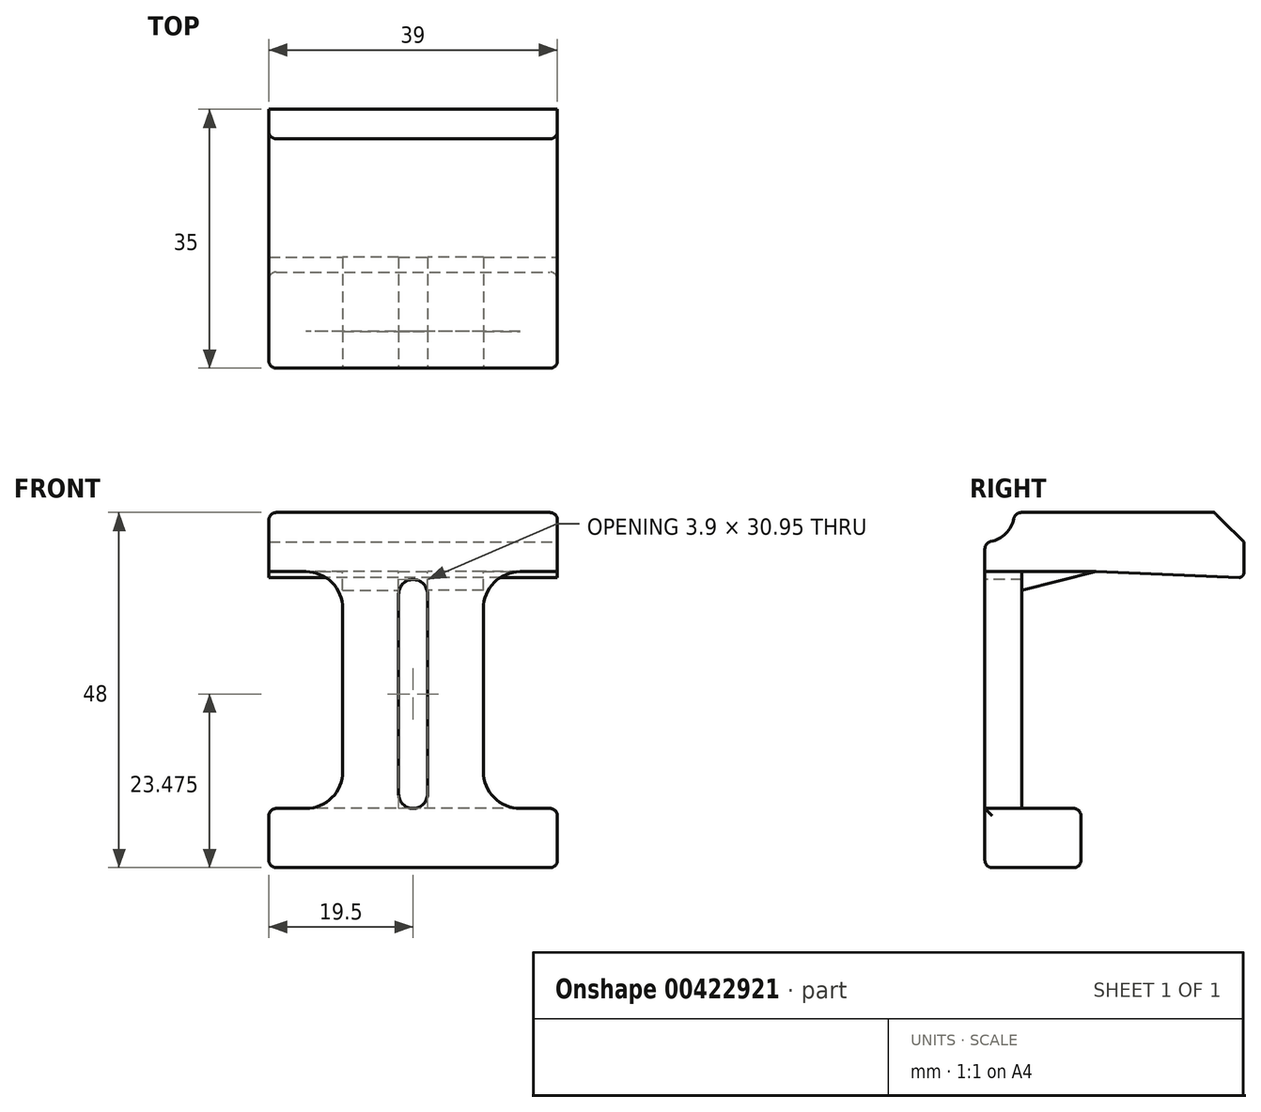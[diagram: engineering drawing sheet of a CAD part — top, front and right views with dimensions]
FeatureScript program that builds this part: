
annotation { "Feature Type Name" : "Feature", "Feature Type Description" : "" }
export const myFeature = defineFeature(function(context is Context, id is Id, definition is map)
    precondition{}
    {
        {
            var Q0;
            Q0=qCreatedBy(makeId("Front.planeOp"),FACE);
            var sketch = newSketch(context, id + "F0", { "sketchPlane" : qUnion([Q0])});
            skLineSegment(sketch, "E0.bottom", {"start": v(-25, 24) * mm, "end": v(14, 24) * mm});
            skLineSegment(sketch, "E0.top", {"start": v(-25, -24) * mm, "end": v(14, -24) * mm});
            skLineSegment(sketch, "E0.left", {"start": v(-25, 24) * mm, "end": v(-25, -24) * mm});
            skLineSegment(sketch, "E0.right", {"start": v(14, 24) * mm, "end": v(14, -24) * mm});
            skSolve(sketch);
        }
        {
            var Q0;
            Q0 = qSketchRegion(id + "F0", true);
            extrude(context, id + "F1", {"entities" : qUnion([Q0]), "depth" : 5 * mm});
        }
        {
            var Q0;
            Q0=makeQuery(id+"F1.opExtrude","CAP_FACE",FACE,{"disambiguationData":[OSD([sQuery(id+"F0.wireOp",EDGE,"E0.bottom"),sQuery(id+"F0.wireOp",EDGE,"E0.top"),sQuery(id+"F0.wireOp",EDGE,"E0.left"),sQuery(id+"F0.wireOp",EDGE,"E0.right")])],"isStart":false});
            var sketch = newSketch(context, id + "F2", { "sketchPlane" : qUnion([Q0])});
            skLineSegment(sketch, "E1.bottom", {"start": v(-25, 16) * mm, "end": v(-15, 16) * mm});
            skLineSegment(sketch, "E1.top", {"start": v(-25, -16) * mm, "end": v(-15, -16) * mm});
            skLineSegment(sketch, "E1.left", {"start": v(-25, 16) * mm, "end": v(-25, -16) * mm});
            skLineSegment(sketch, "E1.right", {"start": v(-15, 16) * mm, "end": v(-15, -16) * mm});
            skLineSegment(sketch, "E2.bottom", {"start": v(14, 16) * mm, "end": v(4, 16) * mm});
            skLineSegment(sketch, "E2.top", {"start": v(14, -16) * mm, "end": v(4, -16) * mm});
            skLineSegment(sketch, "E2.left", {"start": v(14, 16) * mm, "end": v(14, -16) * mm});
            skLineSegment(sketch, "E2.right", {"start": v(4, 16) * mm, "end": v(4, -16) * mm});
            skSolve(sketch);
        }
        {
            var Q0;
            Q0 = qSketchRegion(id + "F2", true);
            extrude(context, id + "F3", {"entities" : qUnion([Q0]), "operationType" : NewBodyOperationType.REMOVE, "endBound" : BoundingType.THROUGH_ALL, "oppositeDirection" : true, "depth" : 25 * mm});
        }
        {
            var Q0;
            Q0=makeQuery(id+"F1.opExtrude","CAP_FACE",FACE,{"disambiguationData":[OSD([sQuery(id+"F0.wireOp",EDGE,"E0.bottom"),sQuery(id+"F0.wireOp",EDGE,"E0.top"),sQuery(id+"F0.wireOp",EDGE,"E0.left"),sQuery(id+"F0.wireOp",EDGE,"E0.right")])],"isStart":true});
            var sketch = newSketch(context, id + "F4", { "sketchPlane" : qUnion([Q0])});
            skLineSegment(sketch, "E3.bottom", {"start": v(-14, 16) * mm, "end": v(25, 16) * mm});
            skLineSegment(sketch, "E3.top", {"start": v(-14, 24) * mm, "end": v(25, 24) * mm});
            skLineSegment(sketch, "E3.left", {"start": v(-14, 16) * mm, "end": v(-14, 24) * mm});
            skLineSegment(sketch, "E3.right", {"start": v(25, 16) * mm, "end": v(25, 24) * mm});
            skSolve(sketch);
        }
        {
            var Q0;
            Q0 = qSketchRegion(id + "F4", true);
            extrude(context, id + "F5", {"entities" : qUnion([Q0]), "operationType" : NewBodyOperationType.ADD, "depth" : 30 * mm});
        }
        {
            var Q0;
            {var subQ0=sQuery(id+"F0.wireOp",EDGE,"E0.bottom");var subQ1=sQuery(id+"F0.wireOp",EDGE,"E0.right");Q0=makeQuery(id+"F5.boolean.opBoolean","MERGE",FACE,{"derivedFrom":[makeQuery(id+"F3.boolean.opBoolean","SPLIT",FACE,{"disambiguationData":[TD([makeQuery(id+"F1.opExtrude","SWEPT_FACE",FACE,{"disambiguationData":[OSD([subQ0])]})])],"derivedFrom":makeQuery(id+"F1.opExtrude","SWEPT_FACE",FACE,{"disambiguationData":[OSD([subQ1])]})}),makeQuery(id+"F5.opExtrude","SWEPT_FACE",FACE,{"disambiguationData":[OSD([sQuery(id+"F4.wireOp",EDGE,"E3.left")])]})]});}
            var sketch = newSketch(context, id + "F6", { "sketchPlane" : qUnion([Q0])});
            skLineSegment(sketch, "E4", {"start": v(10, 16) * mm, "end": v(30, 16) * mm});
            skLineSegment(sketch, "E5", {"start": v(30, 16) * mm, "end": v(30, 15.2) * mm});
            skLineSegment(sketch, "E6", {"start": v(30, 15.2) * mm, "end": v(10, 16) * mm});
            skSolve(sketch);
        }
        {
            var Q0;
            Q0 = qSketchRegion(id + "F6", true);
            var Q1;
            {var subQ0=sQuery(id+"F0.wireOp",EDGE,"E0.bottom");var subQ2=sQuery(id+"F0.wireOp",EDGE,"E0.left");Q1=makeQuery(id+"F5.boolean.opBoolean","MERGE",FACE,{"derivedFrom":[makeQuery(id+"F3.boolean.opBoolean","SPLIT",FACE,{"disambiguationData":[TD([makeQuery(id+"F1.opExtrude","SWEPT_FACE",FACE,{"disambiguationData":[OSD([subQ0])]})])],"derivedFrom":makeQuery(id+"F1.opExtrude","SWEPT_FACE",FACE,{"disambiguationData":[OSD([subQ2])]})}),makeQuery(id+"F5.opExtrude","SWEPT_FACE",FACE,{"disambiguationData":[OSD([sQuery(id+"F4.wireOp",EDGE,"E3.right")])]})]});}
            extrude(context, id + "F7", {"entities" : qUnion([Q0]), "operationType" : NewBodyOperationType.ADD, "endBound" : BoundingType.UP_TO_SURFACE, "oppositeDirection" : true, "endBoundEntityFace" : qUnion([Q1]), "depth" : 25 * mm});
        }
        {
            var Q0;
            {var subQ0=sQuery(id+"F0.wireOp",EDGE,"E0.bottom");var subQ1=sQuery(id+"F0.wireOp",EDGE,"E0.right");Q0=makeQuery(id+"F7.boolean.opBoolean","MERGE",FACE,{"derivedFrom":[makeQuery(id+"F5.boolean.opBoolean","MERGE",FACE,{"derivedFrom":[makeQuery(id+"F3.boolean.opBoolean","SPLIT",FACE,{"disambiguationData":[TD([makeQuery(id+"F1.opExtrude","SWEPT_FACE",FACE,{"disambiguationData":[OSD([subQ0])]})])],"derivedFrom":makeQuery(id+"F1.opExtrude","SWEPT_FACE",FACE,{"disambiguationData":[OSD([subQ1])]})}),makeQuery(id+"F5.opExtrude","SWEPT_FACE",FACE,{"disambiguationData":[OSD([sQuery(id+"F4.wireOp",EDGE,"E3.left")])]})]}),makeQuery(id+"F7.opExtrude","CAP_FACE",FACE,{"disambiguationData":[OSD([sQuery(id+"F6.wireOp",EDGE,"E4"),sQuery(id+"F6.wireOp",EDGE,"E5"),sQuery(id+"F6.wireOp",EDGE,"E6")])],"isStart":true})]});}
            var sketch = newSketch(context, id + "F8", { "sketchPlane" : qUnion([Q0])});
            skCircle(sketch, "E7", {"center": v(-5, 24) * mm, "radius": 4 * mm});
            skSolve(sketch);
        }
        {
            var Q0;
            Q0 = qSketchRegion(id + "F8", true);
            extrude(context, id + "F9", {"entities" : qUnion([Q0]), "operationType" : NewBodyOperationType.REMOVE, "endBound" : BoundingType.THROUGH_ALL, "oppositeDirection" : true, "depth" : 25 * mm});
        }
        {
            var Q0;
            Q0=makeQuery(id+"F9.boolean.opBoolean","INTERSECT",EDGE,{"derivedFrom":[makeQuery(id+"F5.boolean.opBoolean","MERGE",FACE,{"derivedFrom":[makeQuery(id+"F1.opExtrude","SWEPT_FACE",FACE,{"disambiguationData":[OSD([sQuery(id+"F0.wireOp",EDGE,"E0.bottom")])]}),makeQuery(id+"F5.opExtrude","SWEPT_FACE",FACE,{"disambiguationData":[OSD([sQuery(id+"F4.wireOp",EDGE,"E3.top")])]})]}),makeQuery(id+"F9.opExtrude","SWEPT_FACE",FACE,{"disambiguationData":[OSD([sQuery(id+"F8.wireOp",EDGE,"E7")])]})]});
            var Q1;
            Q1=makeQuery(id+"F9.boolean.opBoolean","INTERSECT",EDGE,{"derivedFrom":[makeQuery(id+"F1.opExtrude","CAP_FACE",FACE,{"disambiguationData":[OSD([sQuery(id+"F0.wireOp",EDGE,"E0.bottom"),sQuery(id+"F0.wireOp",EDGE,"E0.top"),sQuery(id+"F0.wireOp",EDGE,"E0.left"),sQuery(id+"F0.wireOp",EDGE,"E0.right")])],"isStart":false}),makeQuery(id+"F9.opExtrude","SWEPT_FACE",FACE,{"disambiguationData":[OSD([sQuery(id+"F8.wireOp",EDGE,"E7")])]})]});
            fillet(context, id + "F10", {"entities" : qUnion([Q0, Q1]), "radius" : 1 * mm, "tangentPropagation" : true, "allowEdgeOverflow" : false});
        }
        {
            var Q0;
            Q0=makeQuery(id+"F5.opExtrude","CAP_EDGE",EDGE,{"disambiguationData":[OSD([sQuery(id+"F4.wireOp",EDGE,"E3.top")])],"isStart":false});
            chamfer(context, id + "F11", {"entities" : qUnion([Q0]), "width" : 4 * mm, "tangentPropagation" : true});
        }
        {
            var Q0;
            Q0=makeQuery(id+"F1.opExtrude","CAP_FACE",FACE,{"disambiguationData":[OSD([sQuery(id+"F0.wireOp",EDGE,"E0.bottom"),sQuery(id+"F0.wireOp",EDGE,"E0.top"),sQuery(id+"F0.wireOp",EDGE,"E0.left"),sQuery(id+"F0.wireOp",EDGE,"E0.right")])],"isStart":true});
            var sketch = newSketch(context, id + "F12", { "sketchPlane" : qUnion([Q0])});
            skLineSegment(sketch, "E8.bottom", {"start": v(-14, -16) * mm, "end": v(25, -16) * mm});
            skLineSegment(sketch, "E8.top", {"start": v(-14, -24) * mm, "end": v(25, -24) * mm});
            skLineSegment(sketch, "E8.left", {"start": v(-14, -16) * mm, "end": v(-14, -24) * mm});
            skLineSegment(sketch, "E8.right", {"start": v(25, -16) * mm, "end": v(25, -24) * mm});
            skSolve(sketch);
        }
        {
            var Q0;
            Q0 = qSketchRegion(id + "F12", true);
            extrude(context, id + "F13", {"entities" : qUnion([Q0]), "operationType" : NewBodyOperationType.ADD, "depth" : 8 * mm});
        }
        {
            var Q0;
            Q0=makeQuery(id+"F1.opExtrude","CAP_FACE",FACE,{"disambiguationData":[OSD([sQuery(id+"F0.wireOp",EDGE,"E0.bottom"),sQuery(id+"F0.wireOp",EDGE,"E0.top"),sQuery(id+"F0.wireOp",EDGE,"E0.left"),sQuery(id+"F0.wireOp",EDGE,"E0.right")])],"isStart":false});
            var sketch = newSketch(context, id + "F14", { "sketchPlane" : qUnion([Q0])});
            skArc(sketch, "E9", {"start": v(-3.55, 13) * mm, "mid": v(-5.5, 14.95) * mm, "end": v(-7.45, 13) * mm});
            skArc(sketch, "E10", {"start": v(-7.45, -14.05) * mm, "mid": v(-5.5, -16) * mm, "end": v(-3.55, -14.05) * mm});
            skLineSegment(sketch, "E11", {"start": v(-3.55, 13) * mm, "end": v(-3.55, -14.05) * mm});
            skLineSegment(sketch, "E12", {"start": v(-7.45, 13) * mm, "end": v(-7.45, -14.05) * mm});
            skSolve(sketch);
        }
        {
            var Q0;
            Q0 = qSketchRegion(id + "F14", true);
            extrude(context, id + "F15", {"entities" : qUnion([Q0]), "operationType" : NewBodyOperationType.REMOVE, "endBound" : BoundingType.THROUGH_ALL, "oppositeDirection" : true, "depth" : 25 * mm});
        }
        {
            var Q0;
            Q0=makeQuery(id+"F1.opExtrude","CAP_EDGE",EDGE,{"disambiguationData":[OSD([sQuery(id+"F0.wireOp",EDGE,"E0.bottom")])],"isStart":false});
            var Q1;
            Q1=makeQuery(id+"F1.opExtrude","CAP_EDGE",EDGE,{"disambiguationData":[OSD([sQuery(id+"F0.wireOp",EDGE,"E0.top")])],"isStart":false});
            var Q2;
            {var subQ0=sQuery(id+"F0.wireOp",EDGE,"E0.left");var subQ1=sQuery(id+"F0.wireOp",EDGE,"E0.top");Q2=makeQuery(id+"F3.boolean.opBoolean","SPLIT",EDGE,{"disambiguationData":[TD([makeQuery(id+"F1.opExtrude","SWEPT_FACE",FACE,{"disambiguationData":[OSD([subQ1])]})])],"derivedFrom":makeQuery(id+"F1.opExtrude","CAP_EDGE",EDGE,{"disambiguationData":[OSD([subQ0])],"isStart":false})});}
            var Q3;
            {var subQ0=sQuery(id+"F0.wireOp",EDGE,"E0.right");var subQ1=sQuery(id+"F0.wireOp",EDGE,"E0.top");Q3=makeQuery(id+"F3.boolean.opBoolean","SPLIT",EDGE,{"disambiguationData":[TD([makeQuery(id+"F1.opExtrude","SWEPT_FACE",FACE,{"disambiguationData":[OSD([subQ1])]})])],"derivedFrom":makeQuery(id+"F1.opExtrude","CAP_EDGE",EDGE,{"disambiguationData":[OSD([subQ0])],"isStart":false})});}
            var Q4;
            {var subQ0=sQuery(id+"F0.wireOp",EDGE,"E0.bottom");var subQ1=sQuery(id+"F0.wireOp",EDGE,"E0.right");Q4=makeQuery(id+"F3.boolean.opBoolean","SPLIT",EDGE,{"disambiguationData":[TD([makeQuery(id+"F1.opExtrude","SWEPT_FACE",FACE,{"disambiguationData":[OSD([subQ0])]})])],"derivedFrom":makeQuery(id+"F1.opExtrude","CAP_EDGE",EDGE,{"disambiguationData":[OSD([subQ1])],"isStart":false})});}
            var Q5;
            {var subQ0=sQuery(id+"F0.wireOp",EDGE,"E0.bottom");var subQ1=sQuery(id+"F0.wireOp",EDGE,"E0.left");Q5=makeQuery(id+"F3.boolean.opBoolean","SPLIT",EDGE,{"disambiguationData":[TD([makeQuery(id+"F1.opExtrude","SWEPT_FACE",FACE,{"disambiguationData":[OSD([subQ0])]})])],"derivedFrom":makeQuery(id+"F1.opExtrude","CAP_EDGE",EDGE,{"disambiguationData":[OSD([subQ1])],"isStart":false})});}
            var Q6;
            Q6=makeQuery(id+"F5.boolean.opBoolean","MERGE",EDGE,{"derivedFrom":[makeQuery(id+"F1.opExtrude","SWEPT_EDGE",EDGE,{"disambiguationData":[OSD([sQuery(id+"F0.wireOp",EDGE,"E0.bottom"),sQuery(id+"F0.wireOp",EDGE,"E0.left")])]}),makeQuery(id+"F5.opExtrude","SWEPT_EDGE",EDGE,{"disambiguationData":[OSD([sQuery(id+"F4.wireOp",EDGE,"E3.top"),sQuery(id+"F4.wireOp",EDGE,"E3.right")])]})]});
            var Q7;
            Q7=makeQuery(id+"F5.boolean.opBoolean","MERGE",EDGE,{"derivedFrom":[makeQuery(id+"F1.opExtrude","SWEPT_EDGE",EDGE,{"disambiguationData":[OSD([sQuery(id+"F0.wireOp",EDGE,"E0.bottom"),sQuery(id+"F0.wireOp",EDGE,"E0.right")])]}),makeQuery(id+"F5.opExtrude","SWEPT_EDGE",EDGE,{"disambiguationData":[OSD([sQuery(id+"F4.wireOp",EDGE,"E3.top"),sQuery(id+"F4.wireOp",EDGE,"E3.left")])]})]});
            var Q8;
            Q8=makeQuery(id+"F13.boolean.opBoolean","MERGE",EDGE,{"derivedFrom":[makeQuery(id+"F1.opExtrude","SWEPT_EDGE",EDGE,{"disambiguationData":[OSD([sQuery(id+"F0.wireOp",EDGE,"E0.top"),sQuery(id+"F0.wireOp",EDGE,"E0.right")])]}),makeQuery(id+"F13.opExtrude","SWEPT_EDGE",EDGE,{"disambiguationData":[OSD([sQuery(id+"F12.wireOp",EDGE,"E8.top"),sQuery(id+"F12.wireOp",EDGE,"E8.left")])]})]});
            var Q9;
            Q9=makeQuery(id+"F13.boolean.opBoolean","MERGE",EDGE,{"derivedFrom":[makeQuery(id+"F1.opExtrude","SWEPT_EDGE",EDGE,{"disambiguationData":[OSD([sQuery(id+"F0.wireOp",EDGE,"E0.top"),sQuery(id+"F0.wireOp",EDGE,"E0.left")])]}),makeQuery(id+"F13.opExtrude","SWEPT_EDGE",EDGE,{"disambiguationData":[OSD([sQuery(id+"F12.wireOp",EDGE,"E8.top"),sQuery(id+"F12.wireOp",EDGE,"E8.right")])]})]});
            var Q10;
            Q10=makeQuery(id+"F13.opExtrude","CAP_EDGE",EDGE,{"disambiguationData":[OSD([sQuery(id+"F12.wireOp",EDGE,"E8.bottom")])],"isStart":false});
            var Q11;
            Q11=makeQuery(id+"F13.opExtrude","CAP_EDGE",EDGE,{"disambiguationData":[OSD([sQuery(id+"F12.wireOp",EDGE,"E8.top")])],"isStart":false});
            var Q12;
            Q12=makeQuery(id+"F13.opExtrude","CAP_EDGE",EDGE,{"disambiguationData":[OSD([sQuery(id+"F12.wireOp",EDGE,"E8.left")])],"isStart":false});
            var Q13;
            Q13=makeQuery(id+"F13.opExtrude","CAP_EDGE",EDGE,{"disambiguationData":[OSD([sQuery(id+"F12.wireOp",EDGE,"E8.right")])],"isStart":false});
            var Q14;
            Q14=makeQuery(id+"F13.boolean.opBoolean","MERGE",EDGE,{"derivedFrom":[makeQuery(id+"F3.boolean.opBoolean","COPY",EDGE,{"derivedFrom":makeQuery(id+"F3.opExtrude","SWEPT_EDGE",EDGE,{"disambiguationData":[OSD([sQuery(id+"F0.wireOp",EDGE,"E0.left"),sQuery(id+"F2.wireOp",EDGE,"E1.top"),sQuery(id+"F2.wireOp",EDGE,"E1.left")])]})}),makeQuery(id+"F13.opExtrude","SWEPT_EDGE",EDGE,{"disambiguationData":[OSD([sQuery(id+"F12.wireOp",EDGE,"E8.bottom"),sQuery(id+"F12.wireOp",EDGE,"E8.right")])]})]});
            var Q15;
            Q15=makeQuery(id+"F13.boolean.opBoolean","MERGE",EDGE,{"derivedFrom":[makeQuery(id+"F3.boolean.opBoolean","COPY",EDGE,{"derivedFrom":makeQuery(id+"F3.opExtrude","SWEPT_EDGE",EDGE,{"disambiguationData":[OSD([sQuery(id+"F0.wireOp",EDGE,"E0.right"),sQuery(id+"F2.wireOp",EDGE,"E2.top"),sQuery(id+"F2.wireOp",EDGE,"E2.left")])]})}),makeQuery(id+"F13.opExtrude","SWEPT_EDGE",EDGE,{"disambiguationData":[OSD([sQuery(id+"F12.wireOp",EDGE,"E8.bottom"),sQuery(id+"F12.wireOp",EDGE,"E8.left")])]})]});
            fillet(context, id + "F16", {"entities" : qUnion([Q0, Q1, Q2, Q3, Q4, Q5, Q6, Q7, Q8, Q9, Q10, Q11, Q12, Q13, Q14, Q15]), "radius" : 1 * mm, "tangentPropagation" : true, "allowEdgeOverflow" : false});
        }
        {
            var Q0;
            Q0=makeQuery(id+"F3.boolean.opBoolean","COPY",EDGE,{"derivedFrom":makeQuery(id+"F3.opExtrude","SWEPT_EDGE",EDGE,{"disambiguationData":[OSD([sQuery(id+"F2.wireOp",EDGE,"E1.bottom"),sQuery(id+"F2.wireOp",EDGE,"E1.right")])]})});
            var Q1;
            Q1=makeQuery(id+"F3.boolean.opBoolean","COPY",EDGE,{"derivedFrom":makeQuery(id+"F3.opExtrude","SWEPT_EDGE",EDGE,{"disambiguationData":[OSD([sQuery(id+"F2.wireOp",EDGE,"E1.top"),sQuery(id+"F2.wireOp",EDGE,"E1.right")])]})});
            var Q2;
            Q2=makeQuery(id+"F3.boolean.opBoolean","COPY",EDGE,{"derivedFrom":makeQuery(id+"F3.opExtrude","SWEPT_EDGE",EDGE,{"disambiguationData":[OSD([sQuery(id+"F2.wireOp",EDGE,"E2.bottom"),sQuery(id+"F2.wireOp",EDGE,"E2.right")])]})});
            var Q3;
            Q3=makeQuery(id+"F3.boolean.opBoolean","COPY",EDGE,{"derivedFrom":makeQuery(id+"F3.opExtrude","SWEPT_EDGE",EDGE,{"disambiguationData":[OSD([sQuery(id+"F2.wireOp",EDGE,"E2.top"),sQuery(id+"F2.wireOp",EDGE,"E2.right")])]})});
            fillet(context, id + "F17", {"entities" : qUnion([Q0, Q1, Q2, Q3]), "radius" : 5 * mm, "tangentPropagation" : true, "allowEdgeOverflow" : false});
        }
        {
            var Q0;
            Q0=makeQuery(id+"F7.opExtrude","SWEPT_EDGE",EDGE,{"disambiguationData":[OSD([sQuery(id+"F6.wireOp",EDGE,"E5"),sQuery(id+"F6.wireOp",EDGE,"E6")])]});
            fillet(context, id + "F18", {"entities" : qUnion([Q0]), "radius" : .6 * mm, "tangentPropagation" : true, "allowEdgeOverflow" : false});
        }
        {
            var Q0;
            Q0=makeQuery(id+"F1.opExtrude","CAP_FACE",FACE,{"disambiguationData":[OSD([sQuery(id+"F0.wireOp",EDGE,"E0.bottom"),sQuery(id+"F0.wireOp",EDGE,"E0.top"),sQuery(id+"F0.wireOp",EDGE,"E0.left"),sQuery(id+"F0.wireOp",EDGE,"E0.right")])],"isStart":true});
            var sketch = newSketch(context, id + "F19", { "sketchPlane" : qUnion([Q0])});
            skLineSegment(sketch, "E13.bottom", {"start": v(-4, 13.5) * mm, "end": v(3.55, 13.5) * mm});
            skLineSegment(sketch, "E13.top", {"start": v(-4, 16) * mm, "end": v(3.55, 16) * mm});
            skLineSegment(sketch, "E13.left", {"start": v(-4, 13.5) * mm, "end": v(-4, 16) * mm});
            skLineSegment(sketch, "E13.right", {"start": v(3.55, 13.5) * mm, "end": v(3.55, 16) * mm});
            skLineSegment(sketch, "E14.bottom", {"start": v(15, 13.5) * mm, "end": v(7.45, 13.5) * mm});
            skLineSegment(sketch, "E14.top", {"start": v(15, 16) * mm, "end": v(7.45, 16) * mm});
            skLineSegment(sketch, "E14.left", {"start": v(15, 13.5) * mm, "end": v(15, 16) * mm});
            skLineSegment(sketch, "E14.right", {"start": v(7.45, 13.5) * mm, "end": v(7.45, 16) * mm});
            skSolve(sketch);
        }
        {
            var Q0;
            Q0 = qSketchRegion(id + "F19", true);
            extrude(context, id + "F20", {"entities" : qUnion([Q0]), "operationType" : NewBodyOperationType.ADD, "depth" : 10 * mm});
        }
        {
            var Q0;
            Q0=makeQuery(id+"F20.opExtrude","CAP_EDGE",EDGE,{"disambiguationData":[OSD([sQuery(id+"F19.wireOp",EDGE,"E13.bottom")])],"isStart":false});
            chamfer(context, id + "F21", {"entities" : qUnion([Q0]), "chamferType" : ChamferType.TWO_OFFSETS, "width1" : 2.5 * mm, "oppositeDirection" : false, "width2" : 10 * mm, "tangentPropagation" : true});
        }
        {
            var Q0;
            Q0=makeQuery(id+"F20.opExtrude","CAP_EDGE",EDGE,{"disambiguationData":[OSD([sQuery(id+"F19.wireOp",EDGE,"E14.bottom")])],"isStart":false});
            chamfer(context, id + "F22", {"entities" : qUnion([Q0]), "chamferType" : ChamferType.TWO_OFFSETS, "width1" : 10 * mm, "oppositeDirection" : false, "width2" : 2.5 * mm, "tangentPropagation" : true});
        }
    });
